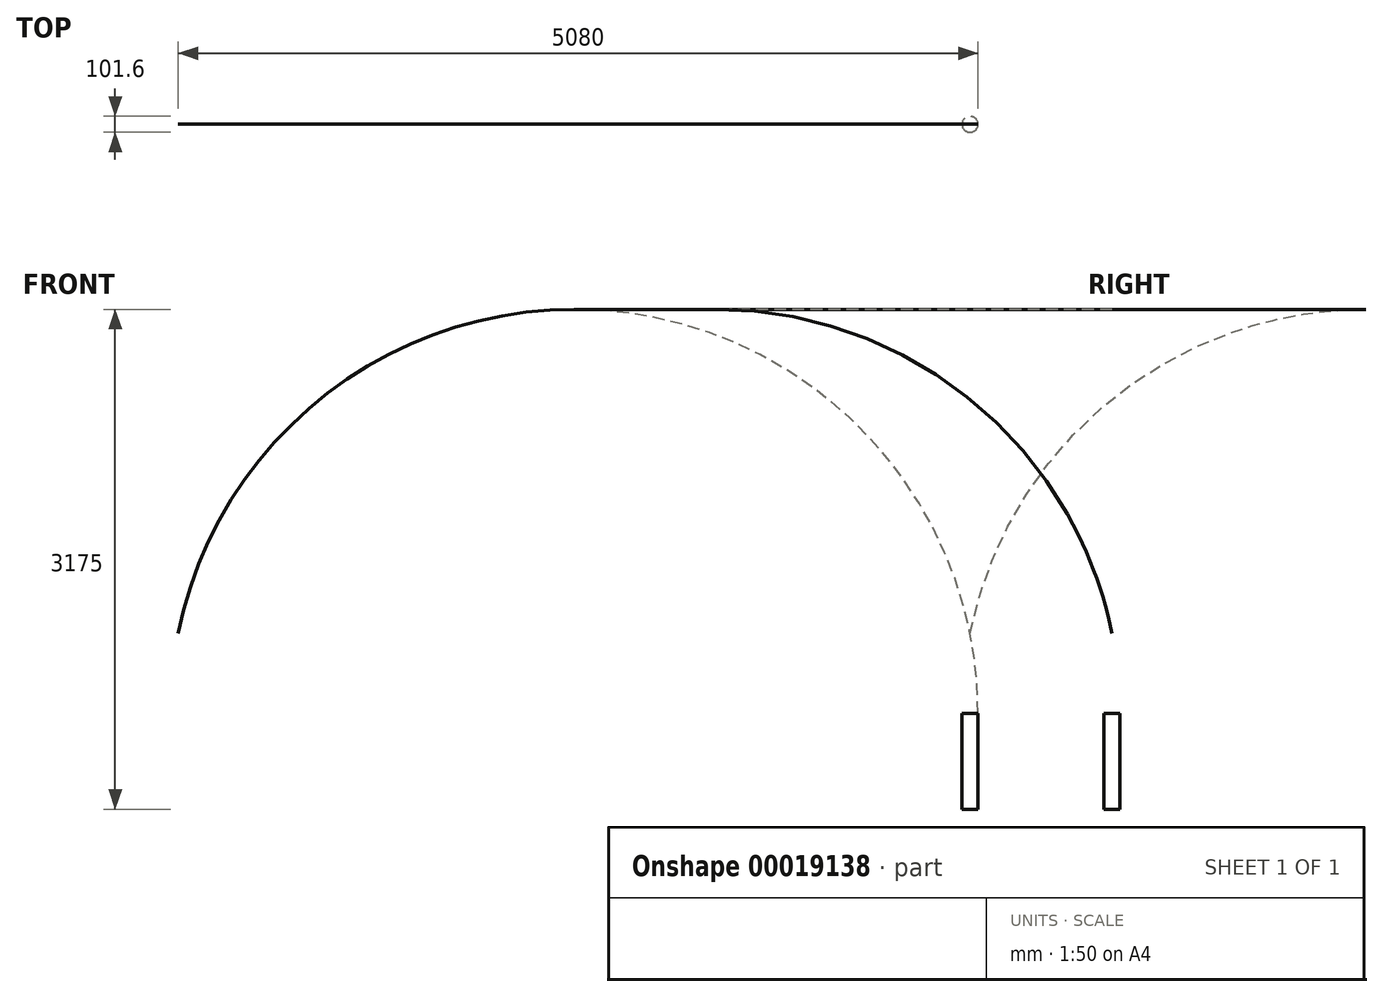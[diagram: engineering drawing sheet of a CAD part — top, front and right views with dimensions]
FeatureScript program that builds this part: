
annotation { "Feature Type Name" : "Feature", "Feature Type Description" : "" }
export const myFeature = defineFeature(function(context is Context, id is Id, definition is map)
    precondition{}
    {
        {
            var Q0;
            Q0=qCreatedBy(makeId("Front.planeOp"),FACE);
            var sketch = newSketch(context, id + "F0", { "sketchPlane" : qUnion([Q0])});
            skLineSegment(sketch, "E0", {"start": v(0, 0) * mm, "end": v(0, 1117.6) * mm});
            skLineSegment(sketch, "E1", {"start": v(0, 0) * mm, "end": v(-50.8, 0) * mm});
            skLineSegment(sketch, "E2", {"start": v(-50.8, 0) * mm, "end": v(-50.8, 609.6) * mm});
            skArc(sketch, "E3", {"start": v(0, 1117.6) * mm, "mid": v(-38.07, 864.87) * mm, "end": v(-50.8, 609.6) * mm});
            skSolve(sketch);
        }
        {
            var Q0;
            Q0=makeQuery(id+"F0.imprint","IMPRINT",FACE,{"disambiguationData":[TD([[makeQuery(id+"F0.imprint","IMPRINT",EDGE,{"derivedFrom":sQuery(id+"F0.wireOp",EDGE,"E0")}),1.0]])]});
            var Q1;
            Q1=sQuery(id+"F0.wireOp",EDGE,"E0");
            revolve(context, id + "F1", {"entities" : qUnion([Q0]), "axis" : qUnion([Q1]), "revolveType" : RevolveType.FULL});
        }
    });
